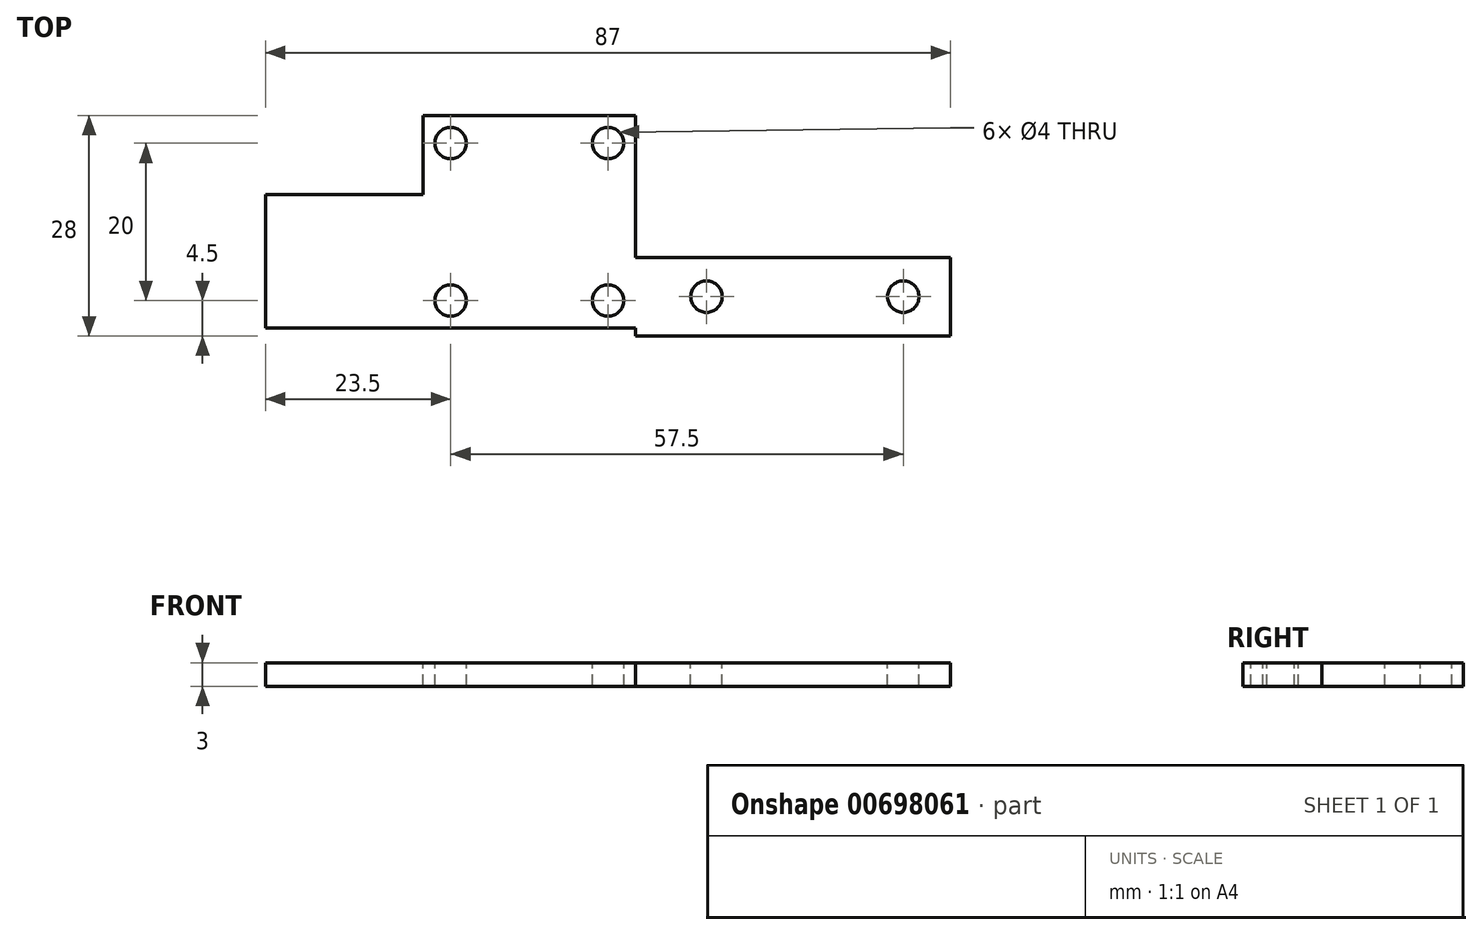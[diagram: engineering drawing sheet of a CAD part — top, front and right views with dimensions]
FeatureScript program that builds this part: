
annotation { "Feature Type Name" : "Feature", "Feature Type Description" : "" }
export const myFeature = defineFeature(function(context is Context, id is Id, definition is map)
    precondition{}
    {
        {
            var Q0;
            Q0=qCreatedBy(makeId("Top.planeOp"),FACE);
            var sketch = newSketch(context, id + "F0", { "sketchPlane" : qUnion([Q0])});
            skLineSegment(sketch, "E0.bottom", {"start": v(13.5, -4) * mm, "end": v(-13.5, -4) * mm});
            skLineSegment(sketch, "E0.top", {"start": v(13.5, 23) * mm, "end": v(-13.5, 23) * mm});
            skLineSegment(sketch, "E0.left", {"start": v(13.5, -4) * mm, "end": v(13.5, 23) * mm});
            skLineSegment(sketch, "E0.right", {"start": v(-13.5, -4) * mm, "end": v(-13.5, 23) * mm});
            skPoint(sketch, "E0.middle", {"position": v(0, 0) * mm});
            skLineSegment(sketch, "E1.bottom", {"start": v(10, -0.5) * mm, "end": v(-10, -0.5) * mm});
            skLineSegment(sketch, "E1.top", {"start": v(10, 19.5) * mm, "end": v(-10, 19.5) * mm});
            skLineSegment(sketch, "E1.left", {"start": v(10, -0.5) * mm, "end": v(10, 19.5) * mm});
            skLineSegment(sketch, "E1.right", {"start": v(-10, -0.5) * mm, "end": v(-10, 19.5) * mm});
            skLineSegment(sketch, "E2.bottom", {"start": v(13.5, 5) * mm, "end": v(53.5, 5) * mm});
            skLineSegment(sketch, "E2.top", {"start": v(13.5, -5) * mm, "end": v(53.5, -5) * mm});
            skLineSegment(sketch, "E2.left", {"start": v(13.5, 5) * mm, "end": v(13.5, -5) * mm});
            skLineSegment(sketch, "E2.right", {"start": v(53.5, 5) * mm, "end": v(53.5, -5) * mm});
            skPoint(sketch, "E2.middle", {"position": v(33.5, 0) * mm});
            skPoint(sketch, "E3.endSnap0", {"position": v(13.5, 0) * mm});
            skLineSegment(sketch, "E4", {"start": v(22.5, 0) * mm, "end": v(47.5, 0) * mm, "construction": true});
            skLineSegment(sketch, "E5.bottom", {"start": v(-13.5, 23) * mm, "end": v(-33.5, 23) * mm});
            skLineSegment(sketch, "E5.top", {"start": v(-13.5, -4) * mm, "end": v(-33.5, -4) * mm});
            skLineSegment(sketch, "E5.left", {"start": v(-13.5, 23) * mm, "end": v(-13.5, -4) * mm});
            skLineSegment(sketch, "E5.right", {"start": v(-33.5, 23) * mm, "end": v(-33.5, -4) * mm});
            skLineSegment(sketch, "E6", {"start": v(0, -0.5) * mm, "end": v(0, -0.5) * mm});
            skLineSegment(sketch, "E7", {"start": v(-10, 9.5) * mm, "end": v(0, 9.5) * mm, "construction": true});
            skLineSegment(sketch, "E8", {"start": v(0, 9.5) * mm, "end": v(10, 9.5) * mm, "construction": true});
            skLineSegment(sketch, "E9", {"start": v(0, 9.5) * mm, "end": v(0, 19.5) * mm, "construction": true});
            skLineSegment(sketch, "E10", {"start": v(0, 9.5) * mm, "end": v(0, -0.5) * mm, "construction": true});
            skLineSegment(sketch, "E11", {"start": v(13.5, 0) * mm, "end": v(22.5, 0) * mm, "construction": true});
            skLineSegment(sketch, "E12.bottom", {"start": v(-13.5, 13) * mm, "end": v(-33.5, 13) * mm});
            skLineSegment(sketch, "E12.top", {"start": v(-13.5, 6) * mm, "end": v(-33.5, 6) * mm});
            skLineSegment(sketch, "E12.left", {"start": v(-13.5, 13) * mm, "end": v(-13.5, 6) * mm});
            skLineSegment(sketch, "E12.right", {"start": v(-33.5, 13) * mm, "end": v(-33.5, 6) * mm});
            skSolve(sketch);
        }
        {
            var Q0;
            Q0=makeQuery(id+"F0.imprint","IMPRINT",FACE,{"disambiguationData":[TD([[makeQuery(id+"F0.imprint","IMPRINT",EDGE,{"derivedFrom":sQuery(id+"F0.wireOp",EDGE,"E1.bottom")}),-1.0]])]});
            var Q1;
            {var subQ4=sQuery(id+"F0.wireOp",EDGE,"E0.bottom");Q1=makeQuery(id+"F0.imprint","IMPRINT",FACE,{"disambiguationData":[TD([[makeQuery(id+"F0.imprint","IMPRINT",EDGE,{"derivedFrom":subQ4}),-1.0]])]});}
            var Q2;
            {var subQ2=sQuery(id+"F0.wireOp",EDGE,"E2.bottom");Q2=makeQuery(id+"F0.imprint","IMPRINT",FACE,{"disambiguationData":[TD([[makeQuery(id+"F0.imprint","IMPRINT",EDGE,{"derivedFrom":subQ2}),-1.0]])]});}
            var Q3;
            {var subQ1=sQuery(id+"F0.wireOp",EDGE,"E2.top");Q3=makeQuery(id+"F0.imprint","IMPRINT",FACE,{"disambiguationData":[TD([[makeQuery(id+"F0.imprint","IMPRINT",EDGE,{"derivedFrom":subQ1}),1.0]])]});}
            extrude(context, id + "F1", {"entities" : qUnion([Q0, Q1, Q2, Q3]), "oppositeDirection" : true, "depth" : 3 * mm, "offsetDistance" : 25 * mm});
        }
        {
            var Q0;
            Q0=sQuery(id+"F0.wireOp",VERTEX,"E1.right.start");
            var Q1;
            Q1=sQuery(id+"F0.wireOp",VERTEX,"E1.right.end");
            var Q2;
            Q2=sQuery(id+"F0.wireOp",VERTEX,"E1.left.start");
            var Q3;
            Q3=sQuery(id+"F0.wireOp",VERTEX,"E4.start");
            var Q4;
            Q4=sQuery(id+"F0.wireOp",VERTEX,"E4.end");
            var Q5;
            Q5=sQuery(id+"F0.wireOp",VERTEX,"E1.top.start");
            var Q6;
            Q6=makeQuery(id+"F1.opExtrude","SWEPT_BODY",BODY,{"disambiguationData":[OSD([sQuery(id+"F0.wireOp",EDGE,"E0.bottom"),sQuery(id+"F0.wireOp",EDGE,"E0.top"),sQuery(id+"F0.wireOp",EDGE,"E0.left"),sQuery(id+"F0.wireOp",EDGE,"E0.right"),sQuery(id+"F0.wireOp",EDGE,"E2.bottom"),sQuery(id+"F0.wireOp",EDGE,"E2.top"),sQuery(id+"F0.wireOp",EDGE,"E2.right")])]});
            hole(context, id + "F2", {"style" : HoleStyle.SIMPLE, "endStyle" : HoleEndStyle.THROUGH, "holeDiameter" : 4 * mm, "majorDiameter" : 5 * mm, "isTappedThrough" : true, "tappedDepth" : 12 * mm, "tapClearance" : 3, "locations" : qUnion([Q0, Q1, Q2, Q3, Q4, Q5]), "scope" : qUnion([Q6])});
        }
        {
            var Q0;
            Q0=makeQuery(id+"F0.imprint","IMPRINT",FACE,{"disambiguationData":[TD([[makeQuery(id+"F0.imprint","IMPRINT",EDGE,{"derivedFrom":sQuery(id+"F0.wireOp",EDGE,"E12.bottom")}),1.0]])]});
            var Q1;
            {var subQ0=sQuery(id+"F0.wireOp",EDGE,"E5.top");Q1=makeQuery(id+"F0.imprint","IMPRINT",FACE,{"disambiguationData":[TD([[makeQuery(id+"F0.imprint","IMPRINT",EDGE,{"derivedFrom":subQ0}),-1.0]])]});}
            extrude(context, id + "F3", {"entities" : qUnion([Q0, Q1]), "operationType" : NewBodyOperationType.ADD, "oppositeDirection" : true, "depth" : 3 * mm, "offsetDistance" : 25 * mm});
        }
    });
